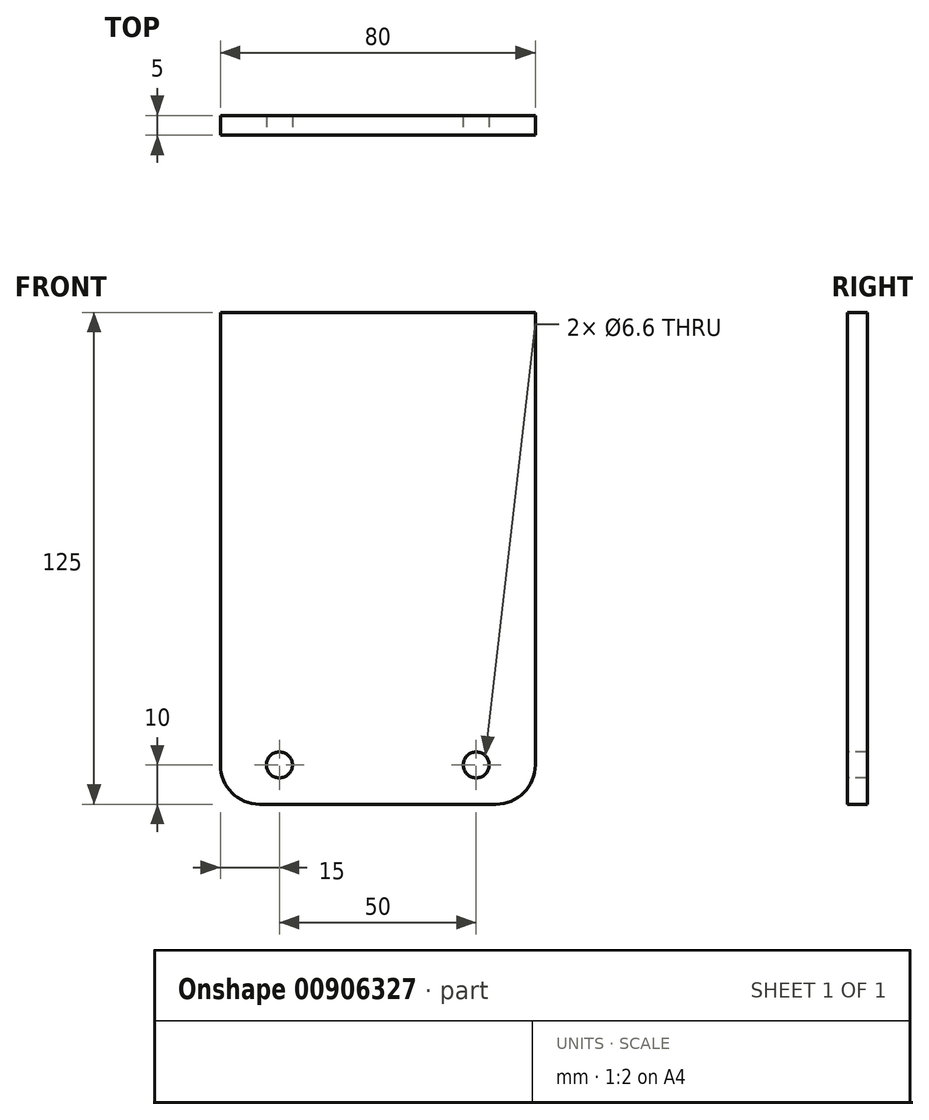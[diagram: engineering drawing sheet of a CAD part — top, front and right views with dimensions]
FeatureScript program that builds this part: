
annotation { "Feature Type Name" : "Feature", "Feature Type Description" : "" }
export const myFeature = defineFeature(function(context is Context, id is Id, definition is map)
    precondition{}
    {
        {
            var Q0;
            Q0=qCreatedBy(makeId("Front.planeOp"),FACE);
            var sketch = newSketch(context, id + "F0", { "sketchPlane" : qUnion([Q0])});
            skLineSegment(sketch, "E0.bottom", {"start": v(40, 62.5) * mm, "end": v(-40, 62.5) * mm});
            skLineSegment(sketch, "E0.top", {"start": v(40, -62.5) * mm, "end": v(-40, -62.5) * mm});
            skLineSegment(sketch, "E0.left", {"start": v(40, 62.5) * mm, "end": v(40, -62.5) * mm});
            skLineSegment(sketch, "E0.right", {"start": v(-40, 62.5) * mm, "end": v(-40, -62.5) * mm});
            skPoint(sketch, "E0.middle", {"position": v(0, 0) * mm});
            skSolve(sketch);
        }
        {
            var Q0;
            Q0=makeQuery(id+"F0.imprint","IMPRINT",FACE,{"disambiguationData":[TD([[makeQuery(id+"F0.imprint","IMPRINT",EDGE,{"derivedFrom":sQuery(id+"F0.wireOp",EDGE,"E0.bottom")}),1.0]])]});
            extrude(context, id + "F1", {"entities" : qUnion([Q0]), "depth" : 5 * mm, "offsetDistance" : 25 * mm});
        }
        {
            var Q0;
            Q0=makeQuery(id+"F1.opExtrude","CAP_FACE",FACE,{"disambiguationData":[OSD([sQuery(id+"F0.wireOp",EDGE,"E0.bottom"),sQuery(id+"F0.wireOp",EDGE,"E0.top"),sQuery(id+"F0.wireOp",EDGE,"E0.left"),sQuery(id+"F0.wireOp",EDGE,"E0.right")])],"isStart":false});
            var sketch = newSketch(context, id + "F2", { "sketchPlane" : qUnion([Q0])});
            skPoint(sketch, "E1", {"position": v(-25, -52.5) * mm});
            skPoint(sketch, "E2", {"position": v(25, -52.5) * mm});
            skSolve(sketch);
        }
        {
            var Q0;
            Q0=sQuery(id+"F2.wireOp",VERTEX,"E1");
            var Q1;
            Q1=sQuery(id+"F2.wireOp",VERTEX,"E2");
            var Q2;
            Q2=makeQuery(id+"F1.opExtrude","SWEPT_BODY",BODY,{"disambiguationData":[OSD([sQuery(id+"F0.wireOp",EDGE,"E0.bottom"),sQuery(id+"F0.wireOp",EDGE,"E0.top"),sQuery(id+"F0.wireOp",EDGE,"E0.left"),sQuery(id+"F0.wireOp",EDGE,"E0.right")])]});
            hole(context, id + "F3", {"style" : HoleStyle.SIMPLE, "endStyle" : HoleEndStyle.THROUGH, "standardTappedOrClearance" : lookupTablePath({ "fit" : "Normal", "standard" : "ISO", "size" : "M6", "type" : "Clearance" }), "standardBlindInLast" : lookupTablePath({ "fit" : "Normal", "standard" : "ISO", "size" : "M6", "type" : "Clearance" }), "holeDiameter" : 6.6 * mm, "majorDiameter" : 5 * mm, "isTappedThrough" : true, "tappedDepth" : 12 * mm, "tapClearance" : 3, "locations" : qUnion([Q0, Q1]), "scope" : qUnion([Q2])});
        }
        {
            var Q0;
            Q0=makeQuery(id+"F1.opExtrude","SWEPT_EDGE",EDGE,{"disambiguationData":[OSD([sQuery(id+"F0.wireOp",EDGE,"E0.top"),sQuery(id+"F0.wireOp",EDGE,"E0.left")])]});
            var Q1;
            Q1=makeQuery(id+"F1.opExtrude","SWEPT_EDGE",EDGE,{"disambiguationData":[OSD([sQuery(id+"F0.wireOp",EDGE,"E0.top"),sQuery(id+"F0.wireOp",EDGE,"E0.right")])]});
            fillet(context, id + "F4", {"entities" : qUnion([Q0, Q1]), "radius" : 10 * mm, "tangentPropagation" : true, "allowEdgeOverflow" : false});
        }
    });
